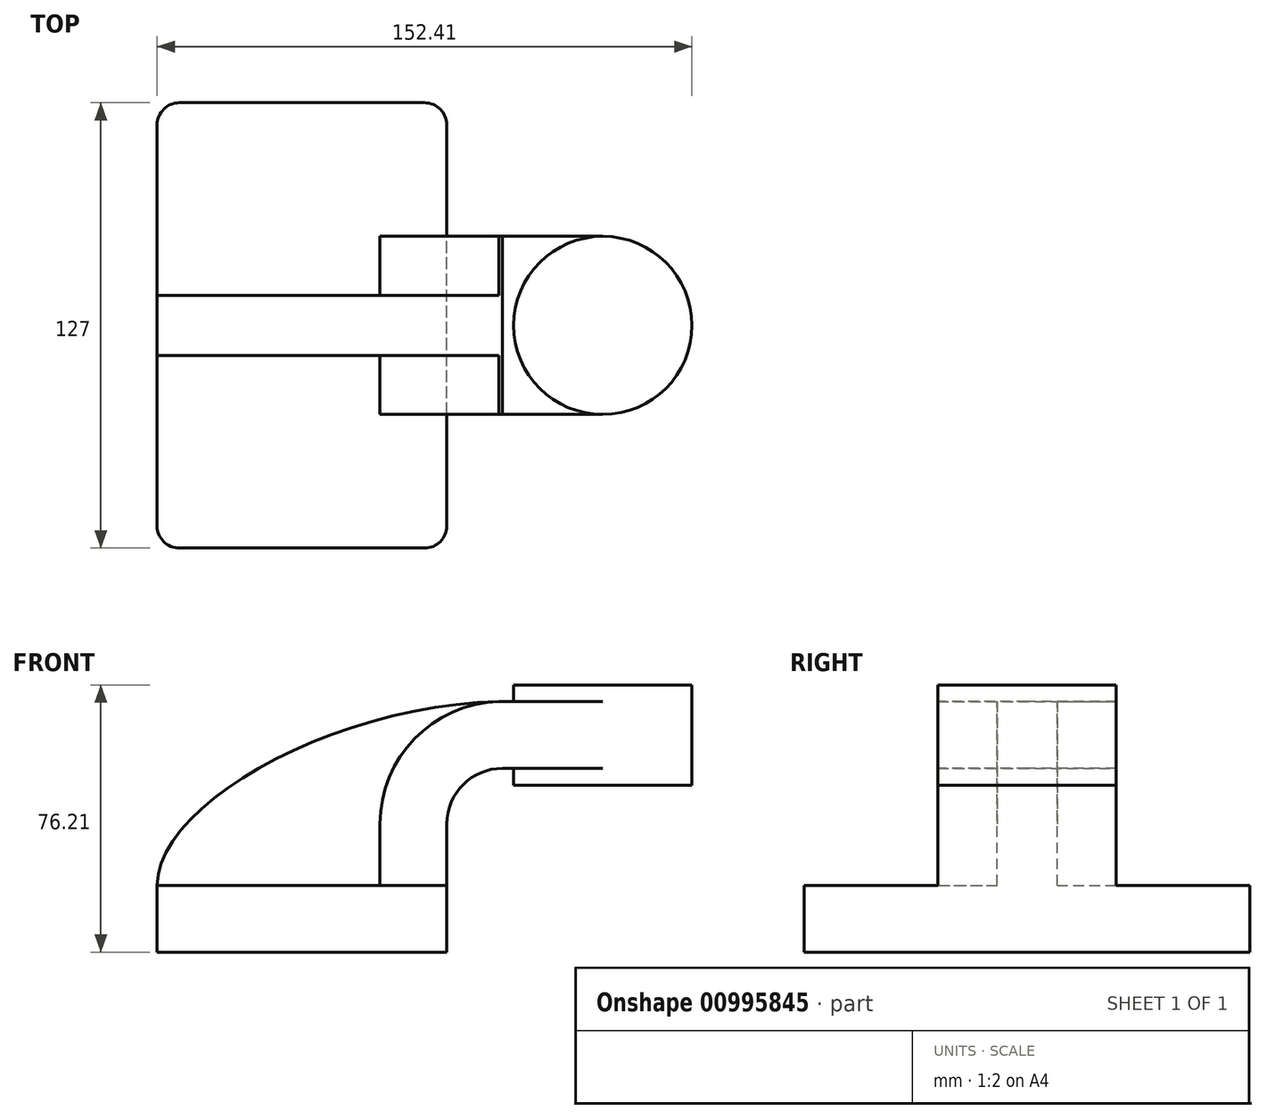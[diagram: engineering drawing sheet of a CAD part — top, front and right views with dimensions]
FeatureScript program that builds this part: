
annotation { "Feature Type Name" : "Feature", "Feature Type Description" : "" }
export const myFeature = defineFeature(function(context is Context, id is Id, definition is map)
    precondition{}
    {
        {
            var Q0;
            Q0=qCreatedBy(makeId("Front.planeOp"),FACE);
            var sketch = newSketch(context, id + "F0", { "sketchPlane" : qUnion([Q0])});
            skLineSegment(sketch, "E0.bottom", {"start": v(-41.28, -9.52) * mm, "end": v(41.28, -9.52) * mm});
            skLineSegment(sketch, "E0.top", {"start": v(-41.28, 9.53) * mm, "end": v(41.28, 9.53) * mm});
            skLineSegment(sketch, "E0.left", {"start": v(-41.28, -9.52) * mm, "end": v(-41.28, 9.53) * mm});
            skLineSegment(sketch, "E0.right", {"start": v(41.28, -9.52) * mm, "end": v(41.28, 9.53) * mm});
            skPoint(sketch, "E0.middle", {"position": v(0, 0) * mm});
            skLineSegment(sketch, "E1.bottom", {"start": v(60.32, 38.1) * mm, "end": v(111.12, 38.1) * mm});
            skLineSegment(sketch, "E1.top", {"start": v(60.32, 66.68) * mm, "end": v(111.12, 66.68) * mm});
            skLineSegment(sketch, "E1.left", {"start": v(60.32, 38.1) * mm, "end": v(60.32, 66.68) * mm});
            skLineSegment(sketch, "E1.right", {"start": v(111.12, 38.1) * mm, "end": v(111.12, 66.68) * mm});
            skPoint(sketch, "E1.middle", {"position": v(85.72, 52.39) * mm});
            skLineSegment(sketch, "E2", {"start": v(41.28, 9.52) * mm, "end": v(41.28, 27) * mm});
            skArc(sketch, "E3", {"start": v(41.27, 27) * mm, "mid": v(45.92, 38.23) * mm, "end": v(57.15, 42.88) * mm});
            skLineSegment(sketch, "E4", {"start": v(57.15, 42.88) * mm, "end": v(85.72, 42.88) * mm});
            skLineSegment(sketch, "E5.0", {"start": v(57.15, 61.93) * mm, "end": v(85.72, 61.93) * mm});
            skArc(sketch, "E5.1", {"start": v(22.22, 27) * mm, "mid": v(32.45, 51.7) * mm, "end": v(57.15, 61.93) * mm});
            skLineSegment(sketch, "E5.2", {"start": v(22.22, 9.52) * mm, "end": v(22.22, 27) * mm});
            skLineSegment(sketch, "E6", {"start": v(85.72, 42.88) * mm, "end": v(85.72, 61.93) * mm});
            skFitSpline(sketch, "E7", {"points": [v(-41.28, 9.53) * mm, v(57.15, 61.93) * mm], "startDerivative": vector(0.13, 70.98) * mm, "endDerivative": vector(139.73, 1.44) * mm});
            skLineSegment(sketch, "E8", {"start": v(85.72, 38.1) * mm, "end": v(85.72, 66.68) * mm});
            skSolve(sketch);
        }
        {
            var Q0;
            Q0=makeQuery(id+"F0.imprint","IMPRINT",FACE,{"disambiguationData":[TD([[makeQuery(id+"F0.imprint","IMPRINT",EDGE,{"derivedFrom":sQuery(id+"F0.wireOp",EDGE,"E0.bottom")}),1.0]])]});
            extrude(context, id + "F1", {"entities" : qUnion([Q0]), "endBound" : BoundingType.SYMMETRIC, "depth" : 127 * mm, "offsetDistance" : 25.4 * mm});
        }
        {
            var Q0;
            {var subQ0=sQuery(id+"F0.wireOp",EDGE,"E2");Q0=makeQuery(id+"F0.imprint","IMPRINT",FACE,{"disambiguationData":[TD([[makeQuery(id+"F0.imprint","IMPRINT",EDGE,{"derivedFrom":subQ0}),1.0]])]});}
            var Q1;
            {var subQ5=sQuery(id+"F0.wireOp",EDGE,"E6");Q1=makeQuery(id+"F0.imprint","IMPRINT",FACE,{"disambiguationData":[TD([[makeQuery(id+"F0.imprint","IMPRINT",EDGE,{"derivedFrom":subQ5}),1.0]])]});}
            var Q2;
            {var subQ0=sQuery(id+"F0.wireOp",EDGE,"E4");var subQ1=sQuery(id+"F0.wireOp",EDGE,"E1.left");var subQ2=makeQuery(id+"F0.imprint","INTERSECT",VERTEX,{"derivedFrom":[subQ1,subQ0]});Q2=makeQuery(id+"F0.imprint","IMPRINT",FACE,{"disambiguationData":[TD([[makeQuery(id+"F0.imprint","IMPRINT",EDGE,{"disambiguationData":[TD([[subQ2,-1.0]])],"derivedFrom":subQ1}),-1.0]])]});}
            extrude(context, id + "F2", {"entities" : qUnion([Q0, Q1, Q2]), "operationType" : NewBodyOperationType.ADD, "endBound" : BoundingType.SYMMETRIC, "depth" : 50.8 * mm, "offsetDistance" : 25.4 * mm});
        }
        {
            var Q0;
            {var subQ3=sQuery(id+"F0.wireOp",EDGE,"E5.2");Q0=makeQuery(id+"F0.imprint","IMPRINT",FACE,{"disambiguationData":[TD([[makeQuery(id+"F0.imprint","IMPRINT",EDGE,{"derivedFrom":subQ3}),1.0]])]});}
            extrude(context, id + "F3", {"entities" : qUnion([Q0]), "operationType" : NewBodyOperationType.ADD, "endBound" : BoundingType.SYMMETRIC, "depth" : 17.14 * mm, "offsetDistance" : 25.4 * mm});
        }
        {
            var Q0;
            {var subQ4=sQuery(id+"F0.wireOp",EDGE,"E1.right");Q0=makeQuery(id+"F0.imprint","IMPRINT",FACE,{"disambiguationData":[TD([[makeQuery(id+"F0.imprint","IMPRINT",EDGE,{"derivedFrom":subQ4}),1.0]])]});}
            var Q1;
            Q1=sQuery(id+"F0.wireOp",EDGE,"E8");
            revolve(context, id + "F4", {"operationType" : NewBodyOperationType.ADD, "surfaceOperationType" : NewSurfaceOperationType.NEW, "entities" : qUnion([Q0]), "axis" : qUnion([Q1]), "revolveType" : RevolveType.FULL});
        }
        {
            var Q0;
            Q0=makeQuery(id+"F1.opExtrude","CAP_EDGE",EDGE,{"disambiguationData":[OSD([sQuery(id+"F0.wireOp",EDGE,"E0.left")])],"isStart":false});
            var Q1;
            Q1=makeQuery(id+"F1.opExtrude","CAP_EDGE",EDGE,{"disambiguationData":[OSD([sQuery(id+"F0.wireOp",EDGE,"E0.right")])],"isStart":false});
            var Q2;
            Q2=makeQuery(id+"F1.opExtrude","CAP_EDGE",EDGE,{"disambiguationData":[OSD([sQuery(id+"F0.wireOp",EDGE,"E0.right")])],"isStart":true});
            var Q3;
            Q3=makeQuery(id+"F1.opExtrude","CAP_EDGE",EDGE,{"disambiguationData":[OSD([sQuery(id+"F0.wireOp",EDGE,"E0.left")])],"isStart":true});
            fillet(context, id + "F5", {"entities" : qUnion([Q0, Q1, Q2, Q3]), "radius" : 6.35 * mm, "tangentPropagation" : true, "allowEdgeOverflow" : false});
        }
    });
